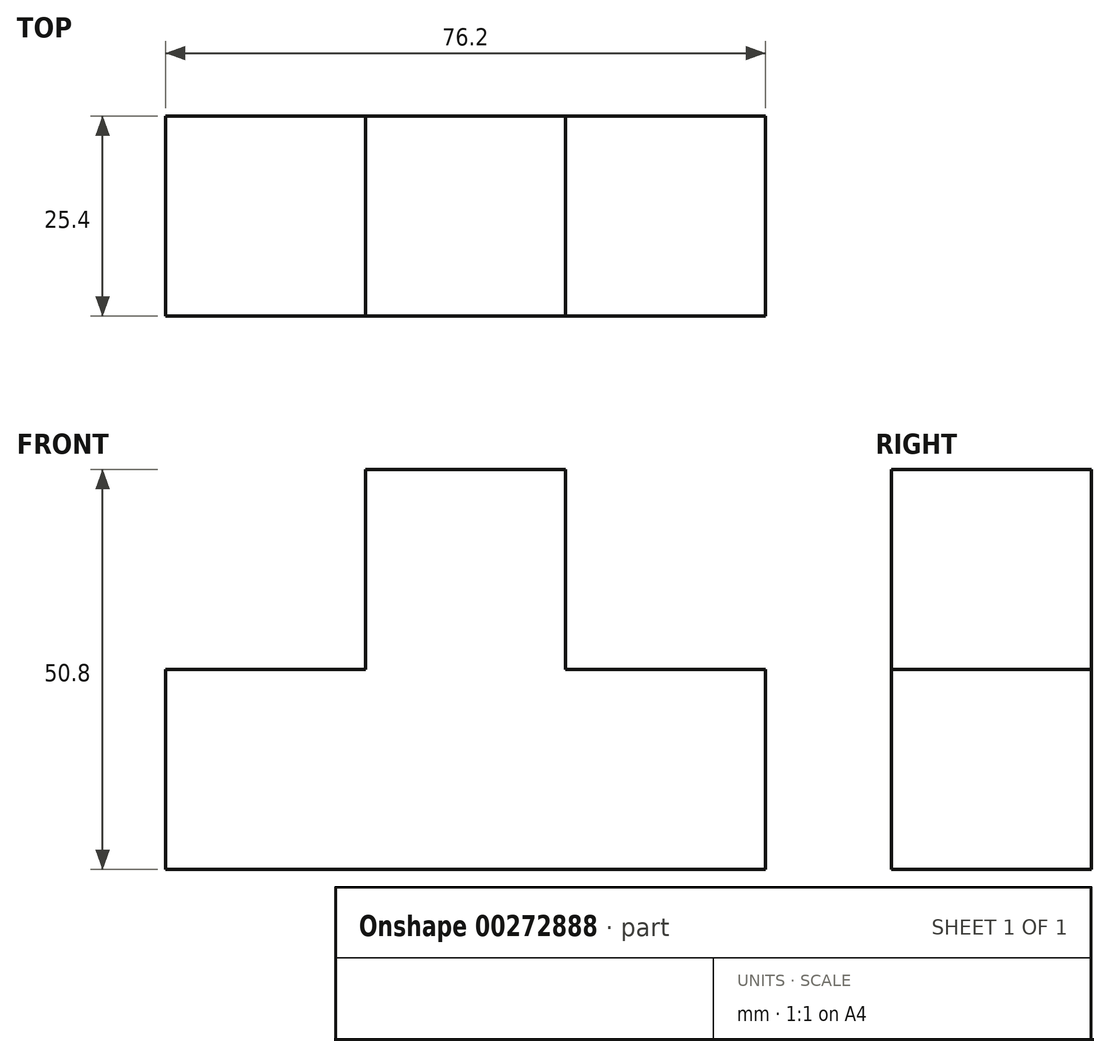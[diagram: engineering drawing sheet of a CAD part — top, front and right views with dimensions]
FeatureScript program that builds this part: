
annotation { "Feature Type Name" : "Feature", "Feature Type Description" : "" }
export const myFeature = defineFeature(function(context is Context, id is Id, definition is map)
    precondition{}
    {
        {
            var Q0;
            Q0=qCreatedBy(makeId("Front.planeOp"),FACE);
            var sketch = newSketch(context, id + "F0", { "sketchPlane" : qUnion([Q0])});
            skLineSegment(sketch, "E0", {"start": v(0, 0) * mm, "end": v(0, 25.4) * mm});
            skLineSegment(sketch, "E1", {"start": v(0, 25.4) * mm, "end": v(-25.4, 25.4) * mm});
            skLineSegment(sketch, "E2", {"start": v(-25.4, 25.4) * mm, "end": v(-25.4, 50.8) * mm});
            skLineSegment(sketch, "E3", {"start": v(-25.4, 50.8) * mm, "end": v(-50.8, 50.8) * mm});
            skLineSegment(sketch, "E4", {"start": v(-50.8, 50.8) * mm, "end": v(-50.8, 25.4) * mm});
            skLineSegment(sketch, "E5", {"start": v(-50.8, 25.4) * mm, "end": v(-76.2, 25.4) * mm});
            skLineSegment(sketch, "E6", {"start": v(-76.2, 25.4) * mm, "end": v(-76.2, 0) * mm});
            skLineSegment(sketch, "E7", {"start": v(-76.2, 0) * mm, "end": v(0, 0) * mm});
            skSolve(sketch);
        }
        {
            var Q0;
            Q0 = qSketchRegion(id + "F0", true);
            extrude(context, id + "F1", {"entities" : qUnion([Q0]), "depth" : 25.4 * mm});
        }
    });
